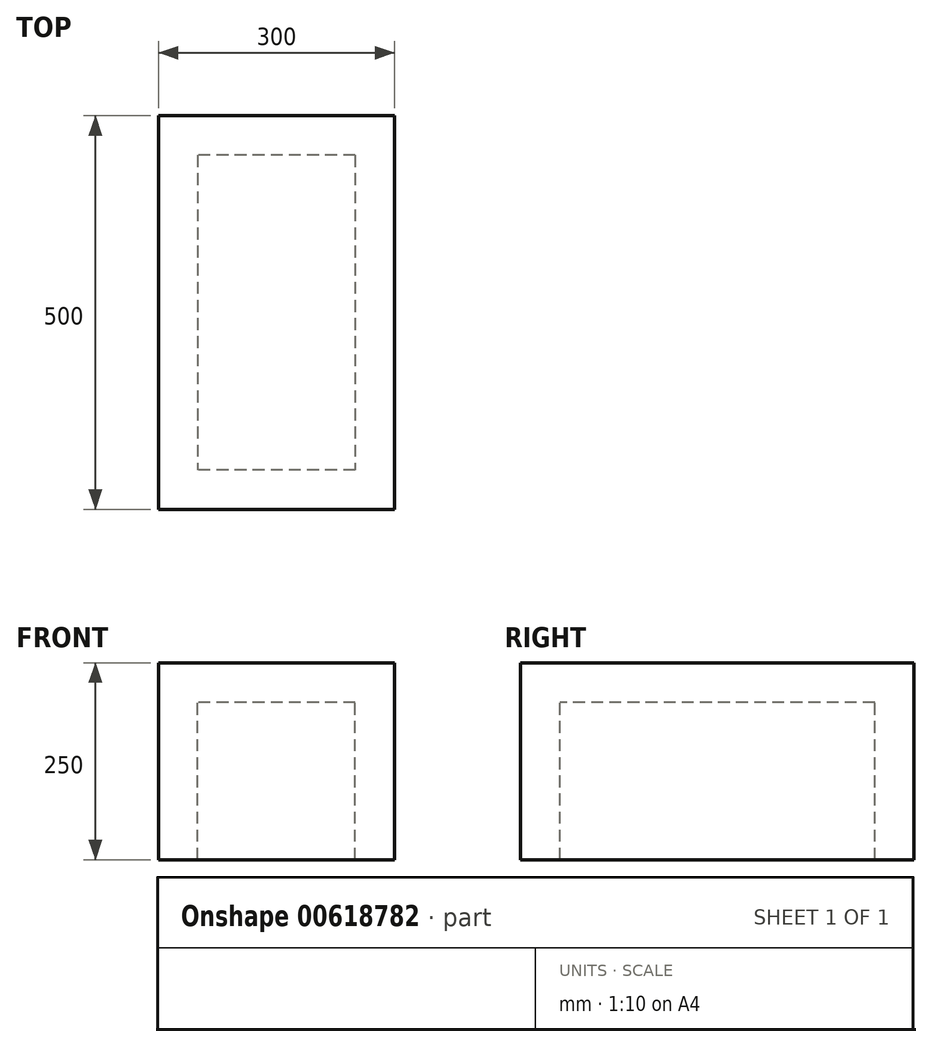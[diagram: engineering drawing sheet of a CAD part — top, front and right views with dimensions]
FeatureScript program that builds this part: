
annotation { "Feature Type Name" : "Feature", "Feature Type Description" : "" }
export const myFeature = defineFeature(function(context is Context, id is Id, definition is map)
    precondition{}
    {
        {
            var Q0;
            Q0=qCreatedBy(makeId("Top.planeOp"),FACE);
            var sketch = newSketch(context, id + "F0", { "sketchPlane" : qUnion([Q0])});
            skLineSegment(sketch, "E0.bottom", {"start": v(150, 250) * mm, "end": v(-150, 250) * mm});
            skLineSegment(sketch, "E0.top", {"start": v(150, -250) * mm, "end": v(-150, -250) * mm});
            skLineSegment(sketch, "E0.left", {"start": v(150, 250) * mm, "end": v(150, -250) * mm});
            skLineSegment(sketch, "E0.right", {"start": v(-150, 250) * mm, "end": v(-150, -250) * mm});
            skPoint(sketch, "E0.middle", {"position": v(0, 0) * mm});
            skSolve(sketch);
        }
        {
            var Q0;
            Q0=makeQuery(id+"F0.imprint","IMPRINT",FACE,{"disambiguationData":[TD([[makeQuery(id+"F0.imprint","IMPRINT",EDGE,{"derivedFrom":sQuery(id+"F0.wireOp",EDGE,"E0.bottom")}),1.0]])]});
            extrude(context, id + "F1", {"entities" : qUnion([Q0]), "oppositeDirection" : true, "depth" : 250 * mm, "offsetDistance" : 25 * mm});
        }
        {
            var Q0;
            Q0=makeQuery(id+"F1.opExtrude","CAP_FACE",FACE,{"disambiguationData":[OSD([sQuery(id+"F0.wireOp",EDGE,"E0.bottom"),sQuery(id+"F0.wireOp",EDGE,"E0.top"),sQuery(id+"F0.wireOp",EDGE,"E0.left"),sQuery(id+"F0.wireOp",EDGE,"E0.right")])],"isStart":false});
            shell(context, id + "F2", {"entities" : qUnion([Q0]), "thickness" : 50 * mm});
        }
    });
